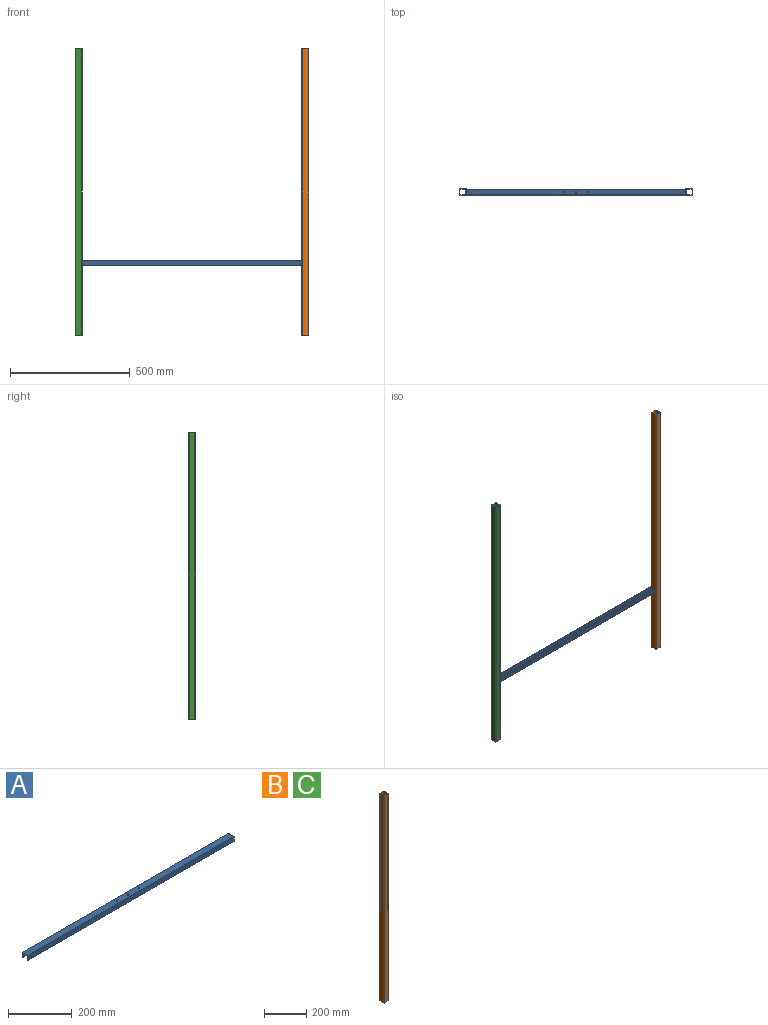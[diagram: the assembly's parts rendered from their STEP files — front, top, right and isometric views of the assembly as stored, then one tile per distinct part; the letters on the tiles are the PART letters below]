
ASSEMBLY  parts=3 mates=2
PART A: 13 faces, bbox 917.6x25.4x19.1 mm
  f0: plane 917.55x22.2mm, normal (0,0,-1), area 20289.3mm2, adj f1,f7,f8,f9,f10,f11,f12
  f1: plane 917.55x17.45mm, normal (0,-1,0), area 16011.2mm2, adj f0,f2,f8,f9
  f2: plane 917.55x1.6mm, normal (0,0,-1), area 1468.1mm2, adj f1,f3,f8,f9
  f3: plane 917.55x19.05mm, normal (0,1,0), area 17479.3mm2, adj f2,f4,f8,f9
  f4: plane 917.55x25.4mm, normal (0,0,1), area 23225.5mm2, adj f3,f5,f8,f9,f10,f11,f12
  f5: plane 917.55x19.05mm, normal (0,-1,0), area 17479.3mm2, adj f4,f6,f8,f9
  f6: plane 917.55x1.6mm, normal (0,0,-1), area 1468.1mm2, adj f5,f7,f8,f9
  f7: plane 917.55x17.45mm, normal (0,1,0), area 16011.2mm2, adj f0,f6,f8,f9
  f8: plane 25.4x19.05mm, normal (1,0,0), area 96.5mm2, adj f0,f1,f2,f3,f4,f5,f6,f7
  f9: plane 25.4x19.05mm, normal (-1,0,0), area 96.5mm2, adj f0,f1,f2,f3,f4,f5,f6,f7
  f10: cylinder r=3.77mm len=7.54mm, axis (0,0,1), area 37.9mm2, adj f0,f4
  f11: cylinder r=2.38mm len=4.76mm, axis (0,0,1), area 23.9mm2, adj f0,f4
  f12: cylinder r=2.38mm len=4.76mm, axis (0,0,1), area 23.9mm2, adj f0,f4
PART B: 18 faces, bbox 28.6x28.6x1197 mm
  f0: plane 1197x22.58mm, normal (0,1,0), area 27022.3mm2, adj f1,f15,f16,f17
  f1: cylinder r=3mm len=1197mm, axis (0,0,1), area 5640.7mm2, adj f0,f2,f16,f17
  f2: plane 1197x22.58mm, normal (-1,0,0), area 27022.3mm2, adj f1,f3,f16,f17
  f3: cylinder r=3mm len=1197mm, axis (0,0,1), area 5640.7mm2, adj f2,f4,f16,f17
  f4: plane 1197x22.58mm, normal (0,-1,0), area 27022.3mm2, adj f3,f5,f16,f17
  f5: cylinder r=3mm len=1197mm, axis (0,0,1), area 5640.7mm2, adj f4,f6,f16,f17
  f6: plane 1197x22.58mm, normal (1,0,0), area 27022.3mm2, adj f5,f15,f16,f17
  f7: cylinder r=1mm len=1197mm, axis (0,0,1), area 1880.2mm2, adj f8,f14,f16,f17
  f8: plane 1197x23.4mm, normal (1,0,0), area 28009.8mm2, adj f7,f9,f16,f17
  f9: cylinder r=1mm len=1197mm, axis (0,0,1), area 1880.2mm2, adj f8,f10,f16,f17
  f10: plane 1197x23.4mm, normal (0,-1,0), area 28009.8mm2, adj f9,f11,f16,f17
  f11: cylinder r=1mm len=1197mm, axis (0,0,1), area 1880.2mm2, adj f10,f12,f16,f17
  f12: plane 1197x23.4mm, normal (-1,0,0), area 28009.8mm2, adj f11,f13,f16,f17
  f13: cylinder r=1mm len=1197mm, axis (0,0,1), area 1880.2mm2, adj f12,f14,f16,f17
  f14: plane 1197x23.4mm, normal (0,1,0), area 28009.8mm2, adj f7,f13,f16,f17
  f15: cylinder r=3mm len=1197mm, axis (0,0,1), area 5640.7mm2, adj f0,f6,f16,f17
  f16: plane 28.58x28.58mm, normal (0,0,-1), area 164.5mm2, adj f0,f1,f2,f3,f4,f5,f6,f7
  f17: plane 28.58x28.58mm, normal (0,0,1), area 164.5mm2, adj f0,f1,f2,f3,f4,f5,f6,f7
PART C: same geometry as B
PLACE A rot(axis=(1,0,0),180deg) t=(0,0,9.53)mm
PLACE B t=(473.06,0,904.81)mm
PLACE C t=(-473.06,0,904.81)mm
MATE fastened C.f6 <-> A.f9  axis (1,0,0) through (-458.78,0,306.31)mm
MATE fastened A.f8 <-> B.f2  axis (1,0,0) through (458.78,0,6.31)mm
